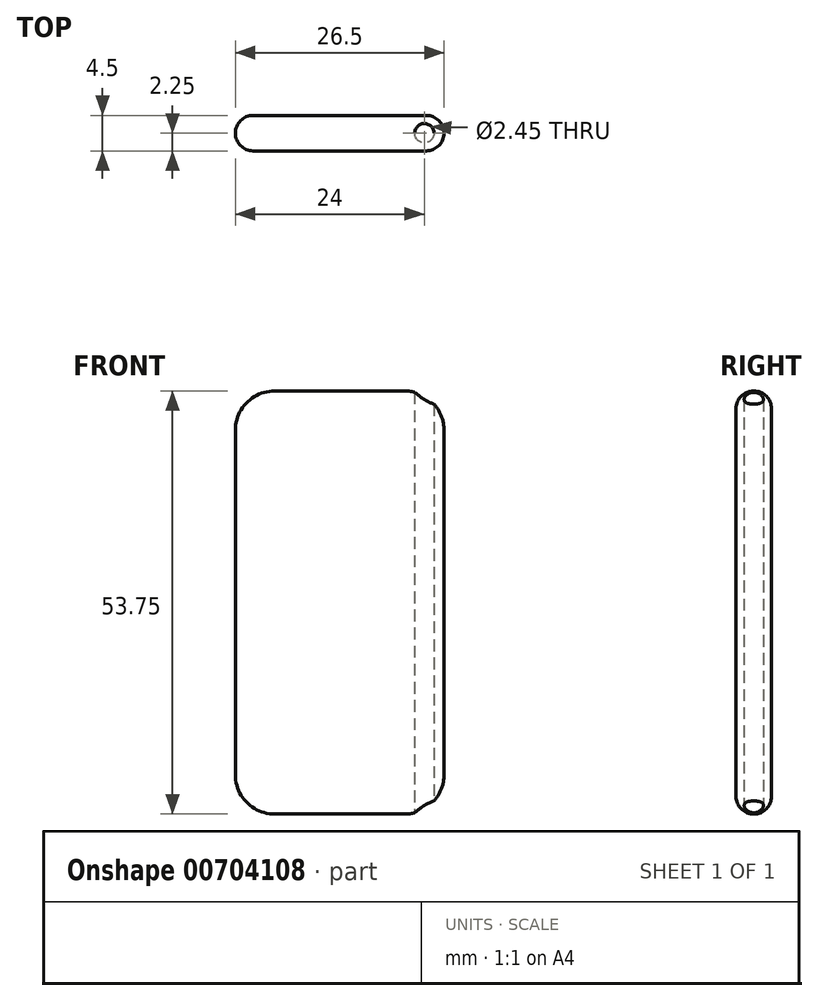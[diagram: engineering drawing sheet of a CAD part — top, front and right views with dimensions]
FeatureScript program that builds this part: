
annotation { "Feature Type Name" : "Feature", "Feature Type Description" : "" }
export const myFeature = defineFeature(function(context is Context, id is Id, definition is map)
    precondition{}
    {
        {
            var Q0;
            Q0=qCreatedBy(makeId("Front.planeOp"),FACE);
            var sketch = newSketch(context, id + "F0", { "sketchPlane" : qUnion([Q0])});
            skLineSegment(sketch, "E0.bottom", {"start": v(5, 0) * mm, "end": v(21.5, 0) * mm});
            skLineSegment(sketch, "E0.top", {"start": v(5, 53.75) * mm, "end": v(21.5, 53.75) * mm});
            skLineSegment(sketch, "E0.left", {"start": v(0, 5) * mm, "end": v(0, 48.75) * mm});
            skLineSegment(sketch, "E0.right", {"start": v(26.5, 5) * mm, "end": v(26.5, 48.75) * mm});
            skPoint(sketch, "E1.visualSharp", {"position": v(26.5, 53.75) * mm});
            skArc(sketch, "E1.filletArc", {"start": v(26.5, 48.75) * mm, "mid": v(25.04, 52.29) * mm, "end": v(21.5, 53.75) * mm});
            skPoint(sketch, "E2.visualSharp", {"position": v(0, 53.75) * mm});
            skArc(sketch, "E2.filletArc", {"start": v(5, 53.75) * mm, "mid": v(1.46, 52.29) * mm, "end": v(0, 48.75) * mm});
            skPoint(sketch, "E3.visualSharp", {"position": v(0, 0) * mm});
            skArc(sketch, "E3.filletArc", {"start": v(0, 5) * mm, "mid": v(1.46, 1.46) * mm, "end": v(5, 0) * mm});
            skPoint(sketch, "E4.visualSharp", {"position": v(26.5, 0) * mm});
            skArc(sketch, "E4.filletArc", {"start": v(21.5, 0) * mm, "mid": v(25.04, 1.46) * mm, "end": v(26.5, 5) * mm});
            skSolve(sketch);
        }
        {
            var Q0;
            Q0=qSketchRegion(id+"F0",true);
            extrude(context, id + "F1", {"entities" : qUnion([Q0]), "depth" : 4.5 * mm});
        }
        {
            var Q0;
            Q0=makeQuery(id+"F1.opExtrude","SWEPT_FACE",FACE,{"disambiguationData":[OSD([sQuery(id+"F0.wireOp",EDGE,"E0.bottom")])]});
            var sketch = newSketch(context, id + "F2", { "sketchPlane" : qUnion([Q0])});
            skCircle(sketch, "E5", {"center": v(24, 2.25) * mm, "radius": 1.23 * mm});
            skSolve(sketch);
        }
        {
            var Q0;
            Q0=qSketchRegion(id+"F2",true);
            var Q1;
            Q1=makeQuery(id+"F1.opExtrude","SWEPT_FACE",FACE,{"disambiguationData":[OSD([sQuery(id+"F0.wireOp",EDGE,"E0.top")])]});
            extrude(context, id + "F3", {"entities" : qUnion([Q0]), "operationType" : NewBodyOperationType.REMOVE, "endBound" : BoundingType.UP_TO_SURFACE, "oppositeDirection" : true, "endBoundEntityFace" : qUnion([Q1]), "depth" : 25 * mm});
        }
        {
            var Q0;
            Q0=makeQuery(id+"F1.opExtrude","CAP_EDGE",EDGE,{"disambiguationData":[OSD([sQuery(id+"F0.wireOp",EDGE,"E0.right")])],"isStart":false});
            var Q1;
            Q1=makeQuery(id+"F1.opExtrude","CAP_EDGE",EDGE,{"disambiguationData":[OSD([sQuery(id+"F0.wireOp",EDGE,"E0.right")])],"isStart":true});
            fillet(context, id + "F4", {"entities" : qUnion([Q0, Q1]), "radius" : 2.25 * mm, "tangentPropagation" : true, "allowEdgeOverflow" : false});
        }
    });
